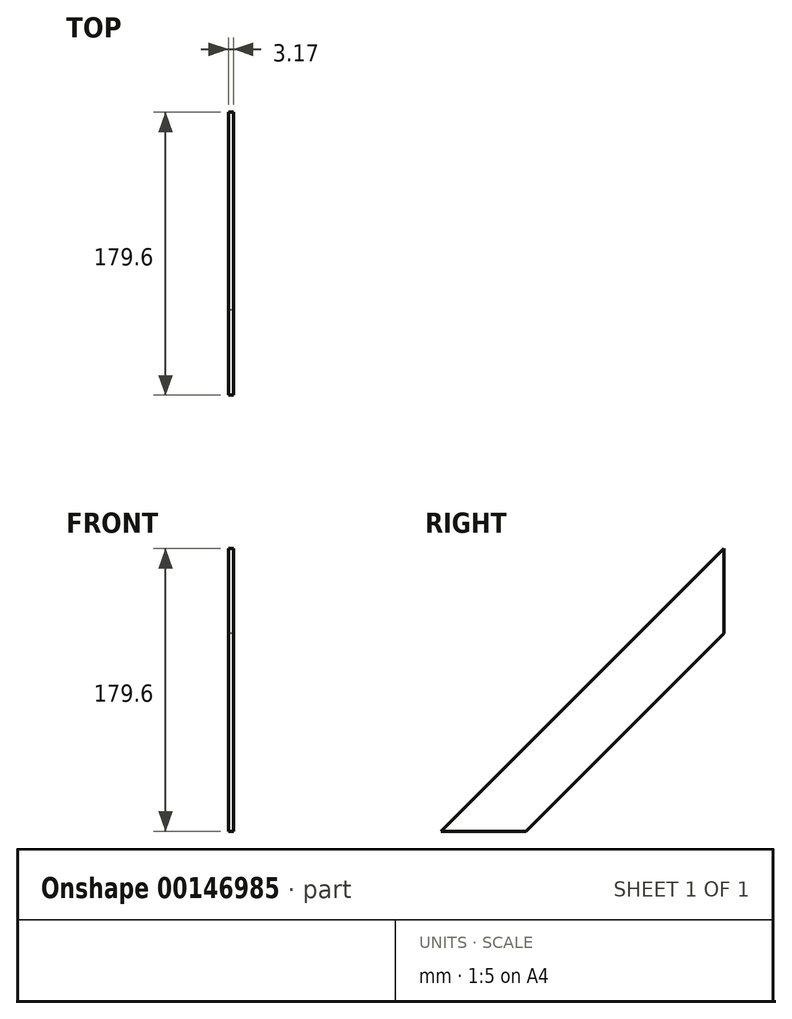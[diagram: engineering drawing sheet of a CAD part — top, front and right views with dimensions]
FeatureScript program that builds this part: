
annotation { "Feature Type Name" : "Feature", "Feature Type Description" : "" }
export const myFeature = defineFeature(function(context is Context, id is Id, definition is map)
    precondition{}
    {
        {
            var Q0;
            Q0=qCreatedBy(makeId("Right.planeOp"),FACE);
            var sketch = newSketch(context, id + "F0", { "sketchPlane" : qUnion([Q0])});
            skLineSegment(sketch, "E0.top", {"start": v(-35.92, -89.8) * mm, "end": v(-89.8, -89.8) * mm});
            skLineSegment(sketch, "E0.left", {"start": v(89.8, 89.8) * mm, "end": v(89.8, 35.92) * mm});
            skPoint(sketch, "E0.middle", {"position": v(0, 0) * mm});
            skLineSegment(sketch, "E1", {"start": v(-89.8, -89.8) * mm, "end": v(89.8, 89.8) * mm});
            skLineSegment(sketch, "E2", {"start": v(-35.92, -89.8) * mm, "end": v(89.8, 35.92) * mm});
            skPoint(sketch, "E0.right.start.orphan", {"position": v(-89.8, 89.8) * mm});
            skPoint(sketch, "E3.orphan", {"position": v(89.8, -89.8) * mm});
            skSolve(sketch);
        }
        {
            var Q0;
            Q0 = qSketchRegion(id + "F0", true);
            extrude(context, id + "F1", {"entities" : qUnion([Q0]), "depth" : 3.17 * mm});
        }
    });
